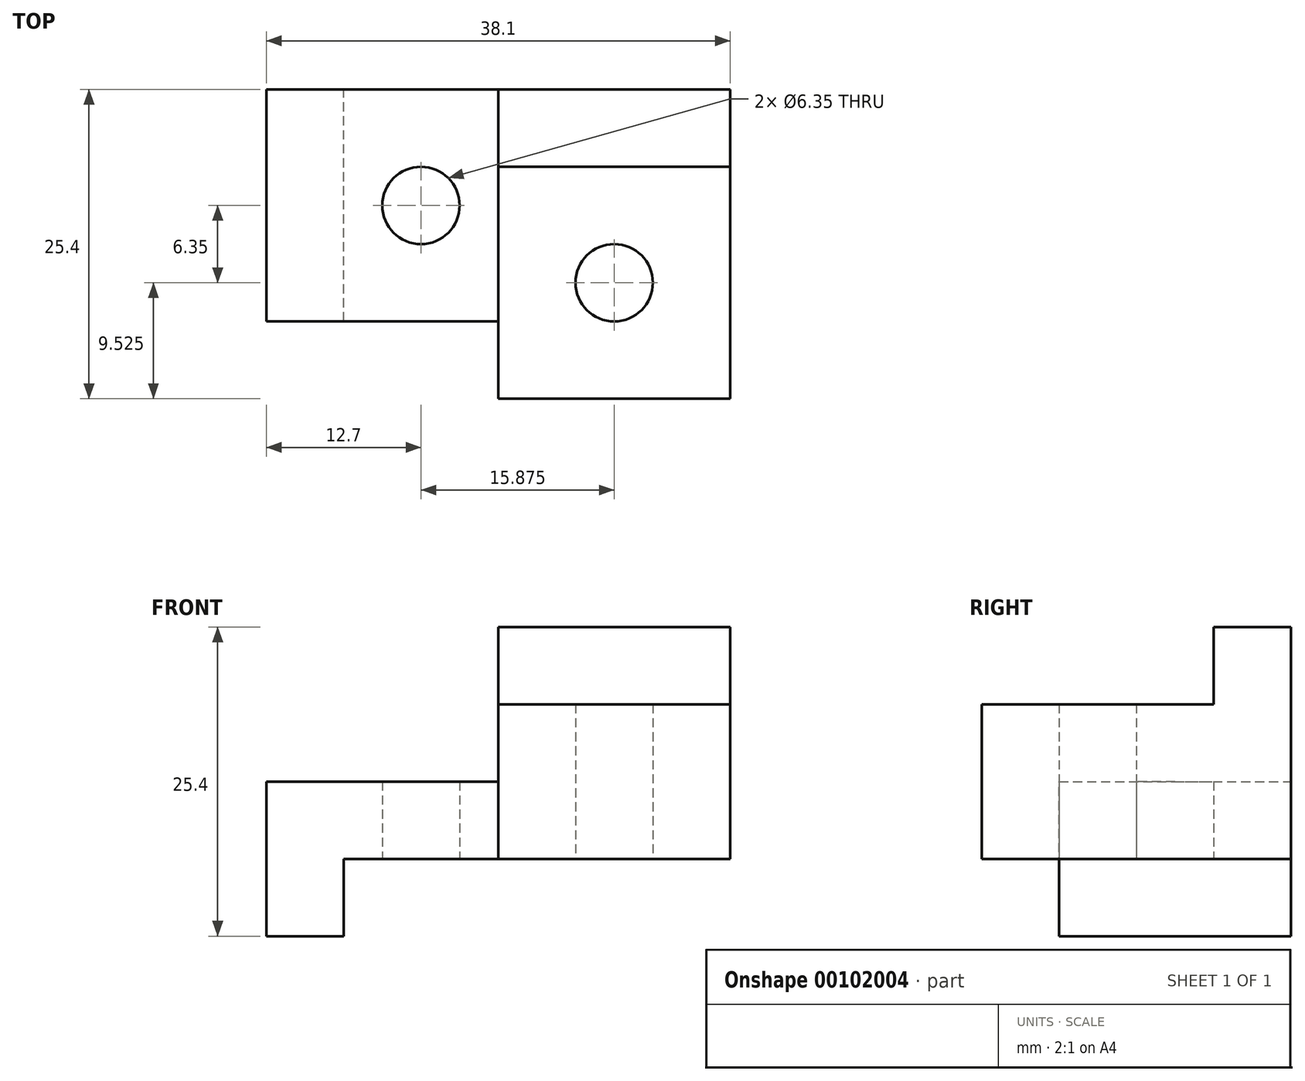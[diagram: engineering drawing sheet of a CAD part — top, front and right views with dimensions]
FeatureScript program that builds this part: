
annotation { "Feature Type Name" : "Feature", "Feature Type Description" : "" }
export const myFeature = defineFeature(function(context is Context, id is Id, definition is map)
    precondition{}
    {
        {
            var Q0;
            Q0=qCreatedBy(makeId("Front.planeOp"),FACE);
            var sketch = newSketch(context, id + "F0", { "sketchPlane" : qUnion([Q0])});
            skLineSegment(sketch, "E0", {"start": v(0, 0) * mm, "end": v(0, 12.7) * mm});
            skLineSegment(sketch, "E1", {"start": v(0, 12.7) * mm, "end": v(38.1, 12.7) * mm});
            skLineSegment(sketch, "E2", {"start": v(38.1, 12.7) * mm, "end": v(38.1, 6.35) * mm});
            skLineSegment(sketch, "E3", {"start": v(38.1, 6.35) * mm, "end": v(6.35, 6.35) * mm});
            skLineSegment(sketch, "E4", {"start": v(6.35, 6.35) * mm, "end": v(6.35, 0) * mm});
            skLineSegment(sketch, "E5", {"start": v(6.35, 0) * mm, "end": v(0, 0) * mm});
            skSolve(sketch);
        }
        {
            var Q0;
            Q0 = qSketchRegion(id + "F0", true);
            extrude(context, id + "F1", {"entities" : qUnion([Q0]), "depth" : 19.05 * mm});
        }
        {
            var Q0;
            Q0=qCreatedBy(makeId("Front.planeOp"),FACE);
            var sketch = newSketch(context, id + "F2", { "sketchPlane" : qUnion([Q0])});
            skLineSegment(sketch, "E6.bottom", {"start": v(38.1, 6.35) * mm, "end": v(19.05, 6.35) * mm});
            skLineSegment(sketch, "E6.top", {"start": v(38.1, 19.05) * mm, "end": v(19.05, 19.05) * mm});
            skLineSegment(sketch, "E6.left", {"start": v(38.1, 6.35) * mm, "end": v(38.1, 19.05) * mm});
            skLineSegment(sketch, "E6.right", {"start": v(19.05, 6.35) * mm, "end": v(19.05, 19.05) * mm});
            skSolve(sketch);
        }
        {
            var Q0;
            Q0 = qSketchRegion(id + "F2", true);
            extrude(context, id + "F3", {"entities" : qUnion([Q0]), "operationType" : NewBodyOperationType.ADD, "depth" : 25.4 * mm});
        }
        {
            var Q0;
            Q0=qCreatedBy(makeId("Front.planeOp"),FACE);
            var sketch = newSketch(context, id + "F4", { "sketchPlane" : qUnion([Q0])});
            skLineSegment(sketch, "E7.bottom", {"start": v(38.1, 19.05) * mm, "end": v(19.05, 19.05) * mm});
            skLineSegment(sketch, "E7.top", {"start": v(38.1, 25.4) * mm, "end": v(19.05, 25.4) * mm});
            skLineSegment(sketch, "E7.left", {"start": v(38.1, 19.05) * mm, "end": v(38.1, 25.4) * mm});
            skLineSegment(sketch, "E7.right", {"start": v(19.05, 19.05) * mm, "end": v(19.05, 25.4) * mm});
            skSolve(sketch);
        }
        {
            var Q0;
            Q0 = qSketchRegion(id + "F4", true);
            extrude(context, id + "F5", {"entities" : qUnion([Q0]), "operationType" : NewBodyOperationType.ADD, "depth" : 6.35 * mm});
        }
        {
            var Q0;
            Q0=qCreatedBy(makeId("Top.planeOp"),FACE);
            var sketch = newSketch(context, id + "F6", { "sketchPlane" : qUnion([Q0])});
            skLineSegment(sketch, "E8", {"start": v(0, 0) * mm, "end": v(12.7, 0) * mm});
            skLineSegment(sketch, "E9", {"start": v(12.7, 0) * mm, "end": v(12.7, -9.53) * mm});
            skLineSegment(sketch, "E10", {"start": v(12.7, 0) * mm, "end": v(28.57, 0) * mm});
            skLineSegment(sketch, "E11", {"start": v(28.57, 0) * mm, "end": v(28.57, -15.88) * mm});
            skCircle(sketch, "E12", {"center": v(12.7, -9.53) * mm, "radius": 3.18 * mm});
            skCircle(sketch, "E13", {"center": v(28.57, -15.88) * mm, "radius": 3.18 * mm});
            skSolve(sketch);
        }
        {
            var Q0;
            Q0 = qSketchRegion(id + "F6", true);
            extrude(context, id + "F7", {"entities" : qUnion([Q0]), "operationType" : NewBodyOperationType.REMOVE, "depth" : 19.05 * mm});
        }
    });
